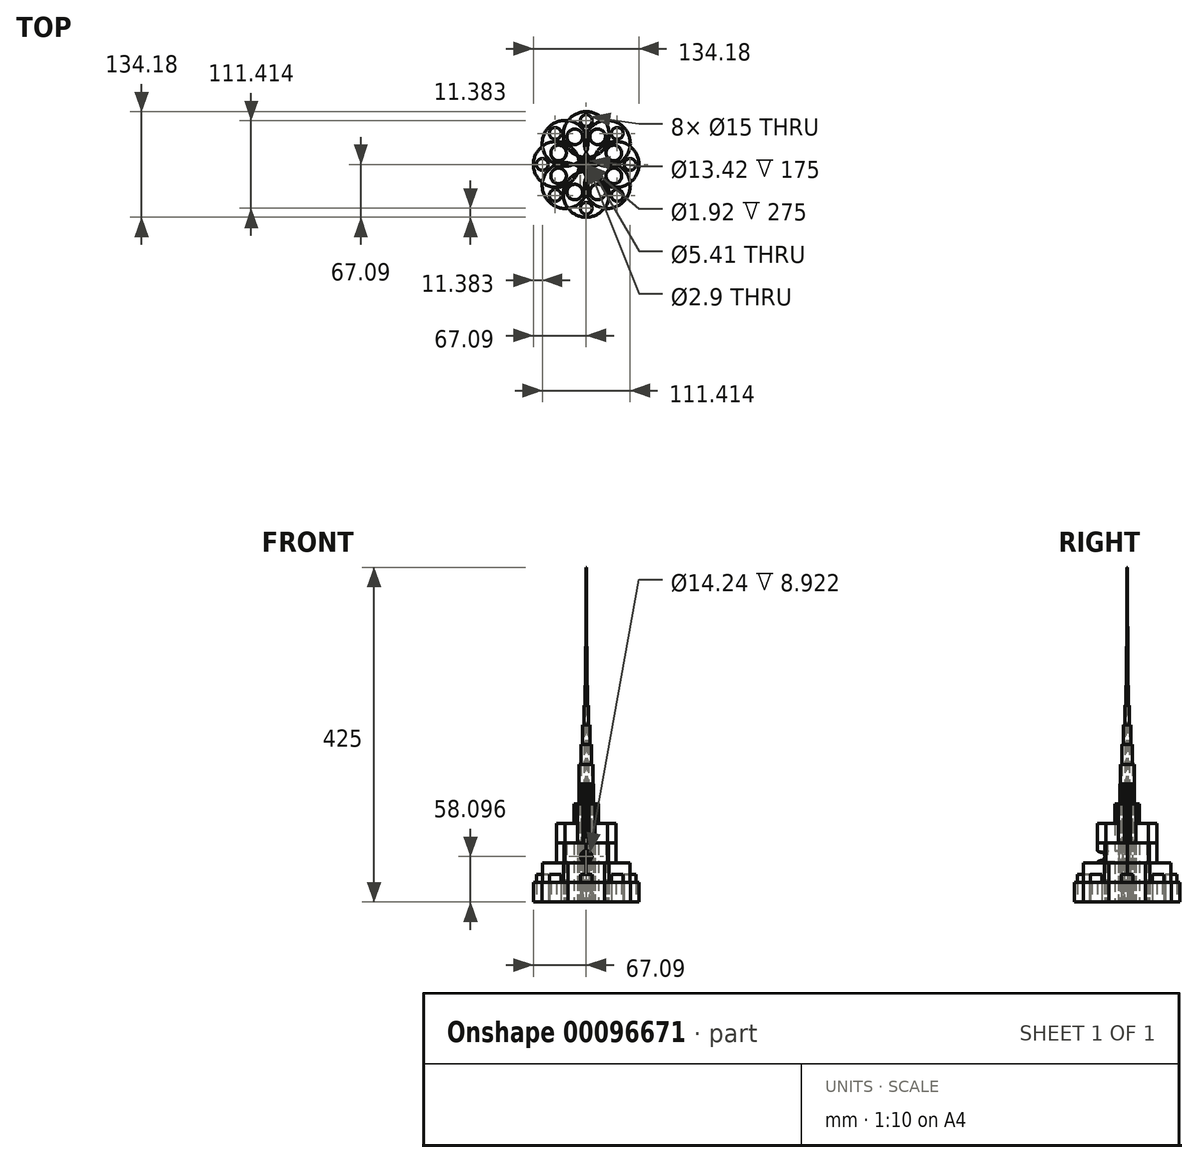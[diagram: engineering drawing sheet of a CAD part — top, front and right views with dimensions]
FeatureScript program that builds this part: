
annotation { "Feature Type Name" : "Feature", "Feature Type Description" : "" }
export const myFeature = defineFeature(function(context is Context, id is Id, definition is map)
    precondition{}
    {
        {
            var Q0;
            Q0=qCreatedBy(makeId("Top.planeOp"),FACE);
            var sketch = newSketch(context, id + "F0", { "sketchPlane" : qUnion([Q0])});
            skCircle(sketch, "E0", {"center": v(0, 0) * mm, "radius": 38 * mm});
            skPoint(sketch, "E1", {"position": v(-26.87, 26.87) * mm});
            skPoint(sketch, "E2", {"position": v(26.87, -26.87) * mm});
            skPoint(sketch, "E3", {"position": v(26.87, 26.87) * mm});
            skPoint(sketch, "E4", {"position": v(-26.87, -26.87) * mm});
            skPoint(sketch, "E5", {"position": v(0, 38) * mm});
            skPoint(sketch, "E6", {"position": v(0, -38) * mm});
            skPoint(sketch, "E7", {"position": v(38, 0) * mm});
            skPoint(sketch, "E8", {"position": v(-38, 0) * mm});
            skCircle(sketch, "E9", {"center": v(-26.87, 26.87) * mm, "radius": 29.08 * mm});
            skCircle(sketch, "E10", {"center": v(26.87, 26.87) * mm, "radius": 29.08 * mm});
            skCircle(sketch, "E11", {"center": v(38, 0) * mm, "radius": 29.08 * mm});
            skCircle(sketch, "E12", {"center": v(-26.87, -26.87) * mm, "radius": 29.08 * mm});
            skCircle(sketch, "E13", {"center": v(26.87, -26.87) * mm, "radius": 29.08 * mm});
            skCircle(sketch, "E14", {"center": v(0, -38) * mm, "radius": 29.08 * mm});
            skCircle(sketch, "E15", {"center": v(-38, 0) * mm, "radius": 29.08 * mm});
            skCircle(sketch, "E16", {"center": v(0, 38) * mm, "radius": 29.08 * mm});
            skCircle(sketch, "E17", {"center": v(0, 0) * mm, "radius": 8.92 * mm});
            skCircle(sketch, "E18", {"center": v(0, 0) * mm, "radius": 6.7 * mm});
            skCircle(sketch, "E19", {"center": v(0, 0) * mm, "radius": 4.58 * mm});
            skCircle(sketch, "E20", {"center": v(0, 0) * mm, "radius": 2.7 * mm});
            skCircle(sketch, "E21", {"center": v(0, 0) * mm, "radius": 1.45 * mm});
            skPoint(sketch, "E22", {"position": v(-23.07, 55.7) * mm});
            skPoint(sketch, "E23", {"position": v(23.07, 55.7) * mm});
            skPoint(sketch, "E24", {"position": v(55.7, 23.07) * mm});
            skPoint(sketch, "E25", {"position": v(55.7, -23.07) * mm});
            skPoint(sketch, "E26", {"position": v(23.07, -55.7) * mm});
            skPoint(sketch, "E27", {"position": v(-23.07, -55.7) * mm});
            skPoint(sketch, "E28", {"position": v(-55.7, -23.07) * mm});
            skPoint(sketch, "E29", {"position": v(-55.7, 23.07) * mm});
            skPoint(sketch, "E30", {"position": v(-14.54, 35.1) * mm});
            skPoint(sketch, "E31", {"position": v(14.54, 35.1) * mm});
            skPoint(sketch, "E32", {"position": v(35.1, 14.54) * mm});
            skPoint(sketch, "E33", {"position": v(35.1, -14.54) * mm});
            skPoint(sketch, "E34", {"position": v(14.54, -35.1) * mm});
            skPoint(sketch, "E35", {"position": v(-14.54, -35.1) * mm});
            skPoint(sketch, "E36", {"position": v(-35.1, -14.54) * mm});
            skPoint(sketch, "E37", {"position": v(-35.1, 14.54) * mm});
            skCircle(sketch, "E38", {"center": v(-35.1, 14.54) * mm, "radius": 9.89 * mm});
            skCircle(sketch, "E39", {"center": v(-14.54, 35.1) * mm, "radius": 9.89 * mm});
            skCircle(sketch, "E40", {"center": v(14.54, 35.1) * mm, "radius": 9.89 * mm});
            skCircle(sketch, "E41", {"center": v(35.1, 14.54) * mm, "radius": 9.89 * mm});
            skCircle(sketch, "E42", {"center": v(35.1, -14.54) * mm, "radius": 9.89 * mm});
            skCircle(sketch, "E43", {"center": v(14.54, -35.1) * mm, "radius": 9.89 * mm});
            skCircle(sketch, "E44", {"center": v(-14.54, -35.1) * mm, "radius": 9.89 * mm});
            skCircle(sketch, "E45", {"center": v(-35.1, -14.54) * mm, "radius": 9.89 * mm});
            skPoint(sketch, "E46", {"position": v(-39.4, 39.4) * mm});
            skPoint(sketch, "E47", {"position": v(0, 55.7) * mm});
            skPoint(sketch, "E48", {"position": v(39.4, 39.4) * mm});
            skPoint(sketch, "E49", {"position": v(55.7, 0) * mm});
            skPoint(sketch, "E50", {"position": v(39.4, -39.4) * mm});
            skPoint(sketch, "E51", {"position": v(0, -55.7) * mm});
            skPoint(sketch, "E52", {"position": v(-39.4, -39.4) * mm});
            skPoint(sketch, "E53", {"position": v(-55.7, 0) * mm});
            skCircle(sketch, "E54", {"center": v(-39.4, 39.4) * mm, "radius": 7.5 * mm});
            skCircle(sketch, "E55", {"center": v(0, 55.7) * mm, "radius": 7.5 * mm});
            skCircle(sketch, "E56", {"center": v(39.4, 39.4) * mm, "radius": 7.5 * mm});
            skCircle(sketch, "E57", {"center": v(55.7, 0) * mm, "radius": 7.5 * mm});
            skCircle(sketch, "E58", {"center": v(39.4, -39.4) * mm, "radius": 7.5 * mm});
            skCircle(sketch, "E59", {"center": v(0, -55.7) * mm, "radius": 7.5 * mm});
            skCircle(sketch, "E60", {"center": v(-39.4, -39.4) * mm, "radius": 7.5 * mm});
            skCircle(sketch, "E61", {"center": v(-55.7, 0) * mm, "radius": 7.5 * mm});
            skCircle(sketch, "E62", {"center": v(0, 0) * mm, "radius": 0.96 * mm});
            skCircle(sketch, "E63", {"center": v(0, 0) * mm, "radius": 0.76 * mm});
            skCircle(sketch, "E64", {"center": v(0, 0) * mm, "radius": 0.57 * mm});
            skCircle(sketch, "E65", {"center": v(0, -0.01) * mm, "radius": 0.41 * mm});
            skCircle(sketch, "E66", {"center": v(0, -0.01) * mm, "radius": 0.3 * mm});
            skCircle(sketch, "E67", {"center": v(0, -0.01) * mm, "radius": 0.19 * mm});
            skSolve(sketch);
        }
        {
            var Q0;
            {var subQ0=sQuery(id+"F0.wireOp",EDGE,"E16");var subQ1=sQuery(id+"F0.wireOp",EDGE,"E9");var subQ2=makeQuery(id+"F0.imprint","INTERSECT",VERTEX,{"disambiguationData":[OD(0.0)],"derivedFrom":[subQ1,subQ0]});Q0=makeQuery(id+"F0.imprint","IMPRINT",FACE,{"disambiguationData":[TD([[makeQuery(id+"F0.imprint","IMPRINT",EDGE,{"disambiguationData":[TD([[subQ2,-1.0]])],"derivedFrom":subQ1}),1.0]])]});}
            var Q1;
            {var subQ0=sQuery(id+"F0.wireOp",EDGE,"E16");var subQ1=sQuery(id+"F0.wireOp",EDGE,"E9");var subQ2=makeQuery(id+"F0.imprint","INTERSECT",VERTEX,{"disambiguationData":[OD(0.0)],"derivedFrom":[subQ1,subQ0]});Q1=makeQuery(id+"F0.imprint","IMPRINT",FACE,{"disambiguationData":[TD([[makeQuery(id+"F0.imprint","IMPRINT",EDGE,{"disambiguationData":[TD([[subQ2,1.0]])],"derivedFrom":subQ0}),1.0]])]});}
            var Q2;
            {var subQ0=sQuery(id+"F0.wireOp",EDGE,"E16");var subQ1=sQuery(id+"F0.wireOp",EDGE,"E10");var subQ2=makeQuery(id+"F0.imprint","INTERSECT",VERTEX,{"disambiguationData":[OD(0.0)],"derivedFrom":[subQ1,subQ0]});Q2=makeQuery(id+"F0.imprint","IMPRINT",FACE,{"disambiguationData":[TD([[makeQuery(id+"F0.imprint","IMPRINT",EDGE,{"disambiguationData":[TD([[subQ2,1.0]])],"derivedFrom":subQ1}),1.0]])]});}
            var Q3;
            {var subQ0=sQuery(id+"F0.wireOp",EDGE,"E11");var subQ1=sQuery(id+"F0.wireOp",EDGE,"E10");var subQ2=makeQuery(id+"F0.imprint","INTERSECT",VERTEX,{"disambiguationData":[OD(0.0)],"derivedFrom":[subQ1,subQ0]});Q3=makeQuery(id+"F0.imprint","IMPRINT",FACE,{"disambiguationData":[TD([[makeQuery(id+"F0.imprint","IMPRINT",EDGE,{"disambiguationData":[TD([[subQ2,1.0]])],"derivedFrom":subQ0}),1.0]])]});}
            var Q4;
            {var subQ0=sQuery(id+"F0.wireOp",EDGE,"E13");var subQ1=sQuery(id+"F0.wireOp",EDGE,"E11");var subQ2=makeQuery(id+"F0.imprint","INTERSECT",VERTEX,{"disambiguationData":[OD(0.0)],"derivedFrom":[subQ1,subQ0]});Q4=makeQuery(id+"F0.imprint","IMPRINT",FACE,{"disambiguationData":[TD([[makeQuery(id+"F0.imprint","IMPRINT",EDGE,{"disambiguationData":[TD([[subQ2,1.0]])],"derivedFrom":subQ0}),1.0]])]});}
            var Q5;
            {var subQ0=sQuery(id+"F0.wireOp",EDGE,"E14");var subQ1=sQuery(id+"F0.wireOp",EDGE,"E12");var subQ2=makeQuery(id+"F0.imprint","INTERSECT",VERTEX,{"disambiguationData":[OD(0.0)],"derivedFrom":[subQ1,subQ0]});Q5=makeQuery(id+"F0.imprint","IMPRINT",FACE,{"disambiguationData":[TD([[makeQuery(id+"F0.imprint","IMPRINT",EDGE,{"disambiguationData":[TD([[subQ2,-1.0]])],"derivedFrom":subQ0}),1.0]])]});}
            var Q6;
            {var subQ0=sQuery(id+"F0.wireOp",EDGE,"E15");var subQ1=sQuery(id+"F0.wireOp",EDGE,"E12");var subQ2=makeQuery(id+"F0.imprint","INTERSECT",VERTEX,{"disambiguationData":[OD(0.0)],"derivedFrom":[subQ1,subQ0]});Q6=makeQuery(id+"F0.imprint","IMPRINT",FACE,{"disambiguationData":[TD([[makeQuery(id+"F0.imprint","IMPRINT",EDGE,{"disambiguationData":[TD([[subQ2,-1.0]])],"derivedFrom":subQ1}),1.0]])]});}
            var Q7;
            {var subQ0=sQuery(id+"F0.wireOp",EDGE,"E15");var subQ1=sQuery(id+"F0.wireOp",EDGE,"E9");var subQ2=makeQuery(id+"F0.imprint","INTERSECT",VERTEX,{"disambiguationData":[OD(0.0)],"derivedFrom":[subQ1,subQ0]});Q7=makeQuery(id+"F0.imprint","IMPRINT",FACE,{"disambiguationData":[TD([[makeQuery(id+"F0.imprint","IMPRINT",EDGE,{"disambiguationData":[TD([[subQ2,-1.0]])],"derivedFrom":subQ0}),1.0]])]});}
            extrude(context, id + "F1", {"entities" : qUnion([Q0, Q1, Q2, Q3, Q4, Q5, Q6, Q7]), "depth" : 25 * mm});
        }
        {
            var Q0;
            {var subQ0=sQuery(id+"F0.wireOp",EDGE,"E9");var subQ3=sQuery(id+"F0.wireOp",EDGE,"E16");var subQ5=makeQuery(id+"F0.imprint","INTERSECT",VERTEX,{"disambiguationData":[OD(0.0)],"derivedFrom":[subQ0,subQ3]});Q0=makeQuery(id+"F0.imprint","IMPRINT",FACE,{"disambiguationData":[TD([[makeQuery(id+"F0.imprint","IMPRINT",EDGE,{"disambiguationData":[TD([[subQ5,1.0]])],"derivedFrom":subQ0}),1.0]])]});}
            var Q1;
            {var subQ0=sQuery(id+"F0.wireOp",EDGE,"E16");var subQ3=sQuery(id+"F0.wireOp",EDGE,"E10");var subQ5=makeQuery(id+"F0.imprint","INTERSECT",VERTEX,{"disambiguationData":[OD(0.0)],"derivedFrom":[subQ3,subQ0]});Q1=makeQuery(id+"F0.imprint","IMPRINT",FACE,{"disambiguationData":[TD([[makeQuery(id+"F0.imprint","IMPRINT",EDGE,{"disambiguationData":[TD([[subQ5,-1.0]])],"derivedFrom":subQ3}),1.0]])]});}
            var Q2;
            {var subQ0=sQuery(id+"F0.wireOp",EDGE,"E13");var subQ3=sQuery(id+"F0.wireOp",EDGE,"E11");var subQ5=makeQuery(id+"F0.imprint","INTERSECT",VERTEX,{"disambiguationData":[OD(0.0)],"derivedFrom":[subQ3,subQ0]});Q2=makeQuery(id+"F0.imprint","IMPRINT",FACE,{"disambiguationData":[TD([[makeQuery(id+"F0.imprint","IMPRINT",EDGE,{"disambiguationData":[TD([[subQ5,1.0]])],"derivedFrom":subQ3}),1.0]])]});}
            var Q3;
            {var subQ0=sQuery(id+"F0.wireOp",EDGE,"E11");var subQ3=sQuery(id+"F0.wireOp",EDGE,"E10");var subQ5=makeQuery(id+"F0.imprint","INTERSECT",VERTEX,{"disambiguationData":[OD(0.0)],"derivedFrom":[subQ3,subQ0]});Q3=makeQuery(id+"F0.imprint","IMPRINT",FACE,{"disambiguationData":[TD([[makeQuery(id+"F0.imprint","IMPRINT",EDGE,{"disambiguationData":[TD([[subQ5,1.0]])],"derivedFrom":subQ3}),1.0]])]});}
            var Q4;
            {var subQ0=sQuery(id+"F0.wireOp",EDGE,"E13");var subQ3=sQuery(id+"F0.wireOp",EDGE,"E14");var subQ5=makeQuery(id+"F0.imprint","INTERSECT",VERTEX,{"disambiguationData":[OD(0.0)],"derivedFrom":[subQ0,subQ3]});Q4=makeQuery(id+"F0.imprint","IMPRINT",FACE,{"disambiguationData":[TD([[makeQuery(id+"F0.imprint","IMPRINT",EDGE,{"disambiguationData":[TD([[subQ5,1.0]])],"derivedFrom":subQ0}),1.0]])]});}
            var Q5;
            {var subQ0=sQuery(id+"F0.wireOp",EDGE,"E14");var subQ3=sQuery(id+"F0.wireOp",EDGE,"E12");var subQ5=makeQuery(id+"F0.imprint","INTERSECT",VERTEX,{"disambiguationData":[OD(0.0)],"derivedFrom":[subQ3,subQ0]});Q5=makeQuery(id+"F0.imprint","IMPRINT",FACE,{"disambiguationData":[TD([[makeQuery(id+"F0.imprint","IMPRINT",EDGE,{"disambiguationData":[TD([[subQ5,-1.0]])],"derivedFrom":subQ3}),1.0]])]});}
            var Q6;
            {var subQ0=sQuery(id+"F0.wireOp",EDGE,"E12");var subQ3=sQuery(id+"F0.wireOp",EDGE,"E15");var subQ5=makeQuery(id+"F0.imprint","INTERSECT",VERTEX,{"disambiguationData":[OD(0.0)],"derivedFrom":[subQ0,subQ3]});Q6=makeQuery(id+"F0.imprint","IMPRINT",FACE,{"disambiguationData":[TD([[makeQuery(id+"F0.imprint","IMPRINT",EDGE,{"disambiguationData":[TD([[subQ5,1.0]])],"derivedFrom":subQ0}),1.0]])]});}
            var Q7;
            {var subQ0=sQuery(id+"F0.wireOp",EDGE,"E15");var subQ3=sQuery(id+"F0.wireOp",EDGE,"E9");var subQ5=makeQuery(id+"F0.imprint","INTERSECT",VERTEX,{"disambiguationData":[OD(0.0)],"derivedFrom":[subQ3,subQ0]});Q7=makeQuery(id+"F0.imprint","IMPRINT",FACE,{"disambiguationData":[TD([[makeQuery(id+"F0.imprint","IMPRINT",EDGE,{"disambiguationData":[TD([[subQ5,-1.0]])],"derivedFrom":subQ3}),1.0]])]});}
            extrude(context, id + "F2", {"entities" : qUnion([Q0, Q1, Q2, Q3, Q4, Q5, Q6, Q7]), "depth" : 50 * mm});
        }
        {
            var Q0;
            {var subQ0=sQuery(id+"F0.wireOp",EDGE,"E16");var subQ5=sQuery(id+"F0.wireOp",EDGE,"E9");var subQ6=makeQuery(id+"F0.imprint","INTERSECT",VERTEX,{"disambiguationData":[OD(1.0)],"derivedFrom":[subQ5,subQ0]});Q0=makeQuery(id+"F0.imprint","IMPRINT",FACE,{"disambiguationData":[TD([[makeQuery(id+"F0.imprint","IMPRINT",EDGE,{"disambiguationData":[TD([[subQ6,-1.0]])],"derivedFrom":subQ5}),1.0]])]});}
            var Q1;
            {var subQ1=sQuery(id+"F0.wireOp",EDGE,"E9");var subQ5=sQuery(id+"F0.wireOp",EDGE,"E12");var subQ6=makeQuery(id+"F0.imprint","INTERSECT",VERTEX,{"derivedFrom":[subQ1,subQ5]});Q1=makeQuery(id+"F0.imprint","IMPRINT",FACE,{"disambiguationData":[TD([[makeQuery(id+"F0.imprint","IMPRINT",EDGE,{"disambiguationData":[TD([[subQ6,-1.0]])],"derivedFrom":subQ1}),1.0]])]});}
            var Q2;
            {var subQ5=sQuery(id+"F0.wireOp",EDGE,"E12");var subQ6=sQuery(id+"F0.wireOp",EDGE,"E9");var subQ7=makeQuery(id+"F0.imprint","INTERSECT",VERTEX,{"derivedFrom":[subQ6,subQ5]});Q2=makeQuery(id+"F0.imprint","IMPRINT",FACE,{"disambiguationData":[TD([[makeQuery(id+"F0.imprint","IMPRINT",EDGE,{"disambiguationData":[TD([[subQ7,1.0]])],"derivedFrom":subQ5}),1.0]])]});}
            var Q3;
            {var subQ0=sQuery(id+"F0.wireOp",EDGE,"E14");var subQ1=sQuery(id+"F0.wireOp",EDGE,"E12");var subQ2=makeQuery(id+"F0.imprint","INTERSECT",VERTEX,{"disambiguationData":[OD(1.0)],"derivedFrom":[subQ1,subQ0]});Q3=makeQuery(id+"F0.imprint","IMPRINT",FACE,{"disambiguationData":[TD([[makeQuery(id+"F0.imprint","IMPRINT",EDGE,{"disambiguationData":[TD([[subQ2,1.0]])],"derivedFrom":subQ1}),1.0]])]});}
            var Q4;
            {var subQ0=sQuery(id+"F0.wireOp",EDGE,"E13");var subQ1=sQuery(id+"F0.wireOp",EDGE,"E12");var subQ2=makeQuery(id+"F0.imprint","INTERSECT",VERTEX,{"derivedFrom":[subQ1,subQ0]});Q4=makeQuery(id+"F0.imprint","IMPRINT",FACE,{"disambiguationData":[TD([[makeQuery(id+"F0.imprint","IMPRINT",EDGE,{"disambiguationData":[TD([[subQ2,1.0]])],"derivedFrom":subQ0}),1.0]])]});}
            var Q5;
            {var subQ0=sQuery(id+"F0.wireOp",EDGE,"E13");var subQ3=sQuery(id+"F0.wireOp",EDGE,"E11");var subQ4=makeQuery(id+"F0.imprint","INTERSECT",VERTEX,{"disambiguationData":[OD(1.0)],"derivedFrom":[subQ3,subQ0]});Q5=makeQuery(id+"F0.imprint","IMPRINT",FACE,{"disambiguationData":[TD([[makeQuery(id+"F0.imprint","IMPRINT",EDGE,{"disambiguationData":[TD([[subQ4,-1.0]])],"derivedFrom":subQ3}),1.0]])]});}
            var Q6;
            {var subQ1=sQuery(id+"F0.wireOp",EDGE,"E10");var subQ5=sQuery(id+"F0.wireOp",EDGE,"E11");var subQ6=makeQuery(id+"F0.imprint","INTERSECT",VERTEX,{"disambiguationData":[OD(1.0)],"derivedFrom":[subQ1,subQ5]});Q6=makeQuery(id+"F0.imprint","IMPRINT",FACE,{"disambiguationData":[TD([[makeQuery(id+"F0.imprint","IMPRINT",EDGE,{"disambiguationData":[TD([[subQ6,-1.0]])],"derivedFrom":subQ1}),1.0]])]});}
            var Q7;
            {var subQ5=sQuery(id+"F0.wireOp",EDGE,"E10");var subQ6=sQuery(id+"F0.wireOp",EDGE,"E9");var subQ7=makeQuery(id+"F0.imprint","INTERSECT",VERTEX,{"derivedFrom":[subQ6,subQ5]});Q7=makeQuery(id+"F0.imprint","IMPRINT",FACE,{"disambiguationData":[TD([[makeQuery(id+"F0.imprint","IMPRINT",EDGE,{"disambiguationData":[TD([[subQ7,-1.0]])],"derivedFrom":subQ5}),1.0]])]});}
            extrude(context, id + "F3", {"entities" : qUnion([Q0, Q1, Q2, Q3, Q4, Q5, Q6, Q7]), "depth" : 75 * mm});
        }
        {
            var Q0;
            {var subQ0=sQuery(id+"F0.wireOp",EDGE,"E10");var subQ1=sQuery(id+"F0.wireOp",EDGE,"E9");var subQ2=makeQuery(id+"F0.imprint","INTERSECT",VERTEX,{"derivedFrom":[subQ1,subQ0]});Q0=makeQuery(id+"F0.imprint","IMPRINT",FACE,{"disambiguationData":[TD([[makeQuery(id+"F0.imprint","IMPRINT",EDGE,{"disambiguationData":[TD([[subQ2,-1.0]])],"derivedFrom":subQ1}),1.0]])]});}
            var Q1;
            {var subQ0=sQuery(id+"F0.wireOp",EDGE,"E16");var subQ1=sQuery(id+"F0.wireOp",EDGE,"E15");var subQ2=makeQuery(id+"F0.imprint","INTERSECT",VERTEX,{"derivedFrom":[subQ1,subQ0]});Q1=makeQuery(id+"F0.imprint","IMPRINT",FACE,{"disambiguationData":[TD([[makeQuery(id+"F0.imprint","IMPRINT",EDGE,{"disambiguationData":[TD([[subQ2,-1.0]])],"derivedFrom":subQ1}),1.0]])]});}
            var Q2;
            {var subQ0=sQuery(id+"F0.wireOp",EDGE,"E12");var subQ1=sQuery(id+"F0.wireOp",EDGE,"E9");var subQ2=makeQuery(id+"F0.imprint","INTERSECT",VERTEX,{"derivedFrom":[subQ1,subQ0]});Q2=makeQuery(id+"F0.imprint","IMPRINT",FACE,{"disambiguationData":[TD([[makeQuery(id+"F0.imprint","IMPRINT",EDGE,{"disambiguationData":[TD([[subQ2,1.0]])],"derivedFrom":subQ1}),1.0]])]});}
            var Q3;
            {var subQ0=sQuery(id+"F0.wireOp",EDGE,"E15");var subQ1=sQuery(id+"F0.wireOp",EDGE,"E14");var subQ2=makeQuery(id+"F0.imprint","INTERSECT",VERTEX,{"derivedFrom":[subQ1,subQ0]});Q3=makeQuery(id+"F0.imprint","IMPRINT",FACE,{"disambiguationData":[TD([[makeQuery(id+"F0.imprint","IMPRINT",EDGE,{"disambiguationData":[TD([[subQ2,-1.0]])],"derivedFrom":subQ1}),1.0]])]});}
            var Q4;
            {var subQ0=sQuery(id+"F0.wireOp",EDGE,"E13");var subQ1=sQuery(id+"F0.wireOp",EDGE,"E12");var subQ2=makeQuery(id+"F0.imprint","INTERSECT",VERTEX,{"derivedFrom":[subQ1,subQ0]});Q4=makeQuery(id+"F0.imprint","IMPRINT",FACE,{"disambiguationData":[TD([[makeQuery(id+"F0.imprint","IMPRINT",EDGE,{"disambiguationData":[TD([[subQ2,1.0]])],"derivedFrom":subQ1}),1.0]])]});}
            var Q5;
            {var subQ0=sQuery(id+"F0.wireOp",EDGE,"E14");var subQ1=sQuery(id+"F0.wireOp",EDGE,"E11");var subQ2=makeQuery(id+"F0.imprint","INTERSECT",VERTEX,{"derivedFrom":[subQ1,subQ0]});Q5=makeQuery(id+"F0.imprint","IMPRINT",FACE,{"disambiguationData":[TD([[makeQuery(id+"F0.imprint","IMPRINT",EDGE,{"disambiguationData":[TD([[subQ2,-1.0]])],"derivedFrom":subQ1}),1.0]])]});}
            var Q6;
            {var subQ0=sQuery(id+"F0.wireOp",EDGE,"E13");var subQ1=sQuery(id+"F0.wireOp",EDGE,"E10");var subQ2=makeQuery(id+"F0.imprint","INTERSECT",VERTEX,{"derivedFrom":[subQ1,subQ0]});Q6=makeQuery(id+"F0.imprint","IMPRINT",FACE,{"disambiguationData":[TD([[makeQuery(id+"F0.imprint","IMPRINT",EDGE,{"disambiguationData":[TD([[subQ2,-1.0]])],"derivedFrom":subQ1}),1.0]])]});}
            var Q7;
            {var subQ0=sQuery(id+"F0.wireOp",EDGE,"E16");var subQ1=sQuery(id+"F0.wireOp",EDGE,"E11");var subQ2=makeQuery(id+"F0.imprint","INTERSECT",VERTEX,{"derivedFrom":[subQ1,subQ0]});Q7=makeQuery(id+"F0.imprint","IMPRINT",FACE,{"disambiguationData":[TD([[makeQuery(id+"F0.imprint","IMPRINT",EDGE,{"disambiguationData":[TD([[subQ2,1.0]])],"derivedFrom":subQ1}),1.0]])]});}
            extrude(context, id + "F4", {"entities" : qUnion([Q0, Q1, Q2, Q3, Q4, Q5, Q6, Q7]), "depth" : 100 * mm});
        }
        {
            var Q0;
            {var subQ0=sQuery(id+"F0.wireOp",EDGE,"E15");var subQ1=sQuery(id+"F0.wireOp",EDGE,"E9");var subQ2=makeQuery(id+"F0.imprint","INTERSECT",VERTEX,{"disambiguationData":[OD(1.0)],"derivedFrom":[subQ1,subQ0]});Q0=makeQuery(id+"F0.imprint","IMPRINT",FACE,{"disambiguationData":[TD([[makeQuery(id+"F0.imprint","IMPRINT",EDGE,{"disambiguationData":[TD([[subQ2,-1.0]])],"derivedFrom":subQ1}),1.0]])]});}
            var Q1;
            {var subQ0=sQuery(id+"F0.wireOp",EDGE,"E16");var subQ1=sQuery(id+"F0.wireOp",EDGE,"E9");var subQ2=makeQuery(id+"F0.imprint","INTERSECT",VERTEX,{"disambiguationData":[OD(1.0)],"derivedFrom":[subQ1,subQ0]});Q1=makeQuery(id+"F0.imprint","IMPRINT",FACE,{"disambiguationData":[TD([[makeQuery(id+"F0.imprint","IMPRINT",EDGE,{"disambiguationData":[TD([[subQ2,-1.0]])],"derivedFrom":subQ1}),-1.0]])]});}
            var Q2;
            {var subQ0=sQuery(id+"F0.wireOp",EDGE,"E16");var subQ1=sQuery(id+"F0.wireOp",EDGE,"E10");var subQ2=makeQuery(id+"F0.imprint","INTERSECT",VERTEX,{"disambiguationData":[OD(1.0)],"derivedFrom":[subQ1,subQ0]});Q2=makeQuery(id+"F0.imprint","IMPRINT",FACE,{"disambiguationData":[TD([[makeQuery(id+"F0.imprint","IMPRINT",EDGE,{"disambiguationData":[TD([[subQ2,-1.0]])],"derivedFrom":subQ1}),1.0]])]});}
            var Q3;
            {var subQ0=sQuery(id+"F0.wireOp",EDGE,"E11");var subQ1=sQuery(id+"F0.wireOp",EDGE,"E10");var subQ2=makeQuery(id+"F0.imprint","INTERSECT",VERTEX,{"disambiguationData":[OD(1.0)],"derivedFrom":[subQ1,subQ0]});Q3=makeQuery(id+"F0.imprint","IMPRINT",FACE,{"disambiguationData":[TD([[makeQuery(id+"F0.imprint","IMPRINT",EDGE,{"disambiguationData":[TD([[subQ2,-1.0]])],"derivedFrom":subQ1}),-1.0]])]});}
            var Q4;
            {var subQ0=sQuery(id+"F0.wireOp",EDGE,"E13");var subQ1=sQuery(id+"F0.wireOp",EDGE,"E11");var subQ2=makeQuery(id+"F0.imprint","INTERSECT",VERTEX,{"disambiguationData":[OD(1.0)],"derivedFrom":[subQ1,subQ0]});Q4=makeQuery(id+"F0.imprint","IMPRINT",FACE,{"disambiguationData":[TD([[makeQuery(id+"F0.imprint","IMPRINT",EDGE,{"disambiguationData":[TD([[subQ2,-1.0]])],"derivedFrom":subQ1}),-1.0]])]});}
            var Q5;
            {var subQ0=sQuery(id+"F0.wireOp",EDGE,"E14");var subQ1=sQuery(id+"F0.wireOp",EDGE,"E12");var subQ2=makeQuery(id+"F0.imprint","INTERSECT",VERTEX,{"disambiguationData":[OD(1.0)],"derivedFrom":[subQ1,subQ0]});Q5=makeQuery(id+"F0.imprint","IMPRINT",FACE,{"disambiguationData":[TD([[makeQuery(id+"F0.imprint","IMPRINT",EDGE,{"disambiguationData":[TD([[subQ2,1.0]])],"derivedFrom":subQ1}),-1.0]])]});}
            var Q6;
            {var subQ0=sQuery(id+"F0.wireOp",EDGE,"E14");var subQ1=sQuery(id+"F0.wireOp",EDGE,"E12");var subQ2=makeQuery(id+"F0.imprint","INTERSECT",VERTEX,{"disambiguationData":[OD(1.0)],"derivedFrom":[subQ1,subQ0]});Q6=makeQuery(id+"F0.imprint","IMPRINT",FACE,{"disambiguationData":[TD([[makeQuery(id+"F0.imprint","IMPRINT",EDGE,{"disambiguationData":[TD([[subQ2,-1.0]])],"derivedFrom":subQ1}),1.0]])]});}
            var Q7;
            {var subQ0=sQuery(id+"F0.wireOp",EDGE,"E12");var subQ1=sQuery(id+"F0.wireOp",EDGE,"E9");var subQ2=makeQuery(id+"F0.imprint","INTERSECT",VERTEX,{"derivedFrom":[subQ1,subQ0]});Q7=makeQuery(id+"F0.imprint","IMPRINT",FACE,{"disambiguationData":[TD([[makeQuery(id+"F0.imprint","IMPRINT",EDGE,{"disambiguationData":[TD([[subQ2,-1.0]])],"derivedFrom":subQ1}),-1.0]])]});}
            extrude(context, id + "F5", {"entities" : qUnion([Q0, Q1, Q2, Q3, Q4, Q5, Q6, Q7]), "depth" : 125 * mm});
        }
        {
            var Q0;
            {var subQ0=sQuery(id+"F0.wireOp",EDGE,"E17");var subQ1=sQuery(id+"F0.wireOp",EDGE,"E9");var subQ2=makeQuery(id+"F0.imprint","INTERSECT",VERTEX,{"derivedFrom":[subQ1,subQ0]});Q0=makeQuery(id+"F0.imprint","IMPRINT",FACE,{"disambiguationData":[TD([[makeQuery(id+"F0.imprint","IMPRINT",EDGE,{"disambiguationData":[TD([[subQ2,-1.0]])],"derivedFrom":subQ1}),-1.0]])]});}
            var Q1;
            {var subQ0=sQuery(id+"F0.wireOp",EDGE,"E16");var subQ1=sQuery(id+"F0.wireOp",EDGE,"E10");var subQ2=makeQuery(id+"F0.imprint","INTERSECT",VERTEX,{"disambiguationData":[OD(1.0)],"derivedFrom":[subQ1,subQ0]});Q1=makeQuery(id+"F0.imprint","IMPRINT",FACE,{"disambiguationData":[TD([[makeQuery(id+"F0.imprint","IMPRINT",EDGE,{"disambiguationData":[TD([[subQ2,-1.0]])],"derivedFrom":subQ1}),-1.0]])]});}
            var Q2;
            {var subQ0=sQuery(id+"F0.wireOp",EDGE,"E15");var subQ1=sQuery(id+"F0.wireOp",EDGE,"E9");var subQ2=makeQuery(id+"F0.imprint","INTERSECT",VERTEX,{"disambiguationData":[OD(1.0)],"derivedFrom":[subQ1,subQ0]});Q2=makeQuery(id+"F0.imprint","IMPRINT",FACE,{"disambiguationData":[TD([[makeQuery(id+"F0.imprint","IMPRINT",EDGE,{"disambiguationData":[TD([[subQ2,-1.0]])],"derivedFrom":subQ1}),-1.0]])]});}
            var Q3;
            {var subQ0=sQuery(id+"F0.wireOp",EDGE,"E17");var subQ1=sQuery(id+"F0.wireOp",EDGE,"E12");var subQ2=makeQuery(id+"F0.imprint","INTERSECT",VERTEX,{"derivedFrom":[subQ1,subQ0]});Q3=makeQuery(id+"F0.imprint","IMPRINT",FACE,{"disambiguationData":[TD([[makeQuery(id+"F0.imprint","IMPRINT",EDGE,{"disambiguationData":[TD([[subQ2,-1.0]])],"derivedFrom":subQ1}),-1.0]])]});}
            var Q4;
            {var subQ0=sQuery(id+"F0.wireOp",EDGE,"E14");var subQ1=sQuery(id+"F0.wireOp",EDGE,"E12");var subQ2=makeQuery(id+"F0.imprint","INTERSECT",VERTEX,{"disambiguationData":[OD(1.0)],"derivedFrom":[subQ1,subQ0]});Q4=makeQuery(id+"F0.imprint","IMPRINT",FACE,{"disambiguationData":[TD([[makeQuery(id+"F0.imprint","IMPRINT",EDGE,{"disambiguationData":[TD([[subQ2,-1.0]])],"derivedFrom":subQ1}),-1.0]])]});}
            var Q5;
            {var subQ0=sQuery(id+"F0.wireOp",EDGE,"E17");var subQ1=sQuery(id+"F0.wireOp",EDGE,"E13");var subQ2=makeQuery(id+"F0.imprint","INTERSECT",VERTEX,{"derivedFrom":[subQ1,subQ0]});Q5=makeQuery(id+"F0.imprint","IMPRINT",FACE,{"disambiguationData":[TD([[makeQuery(id+"F0.imprint","IMPRINT",EDGE,{"disambiguationData":[TD([[subQ2,-1.0]])],"derivedFrom":subQ1}),-1.0]])]});}
            var Q6;
            {var subQ0=sQuery(id+"F0.wireOp",EDGE,"E17");var subQ1=sQuery(id+"F0.wireOp",EDGE,"E11");var subQ2=makeQuery(id+"F0.imprint","INTERSECT",VERTEX,{"derivedFrom":[subQ1,subQ0]});Q6=makeQuery(id+"F0.imprint","IMPRINT",FACE,{"disambiguationData":[TD([[makeQuery(id+"F0.imprint","IMPRINT",EDGE,{"disambiguationData":[TD([[subQ2,-1.0]])],"derivedFrom":subQ1}),-1.0]])]});}
            var Q7;
            {var subQ0=sQuery(id+"F0.wireOp",EDGE,"E17");var subQ1=sQuery(id+"F0.wireOp",EDGE,"E10");var subQ2=makeQuery(id+"F0.imprint","INTERSECT",VERTEX,{"derivedFrom":[subQ1,subQ0]});Q7=makeQuery(id+"F0.imprint","IMPRINT",FACE,{"disambiguationData":[TD([[makeQuery(id+"F0.imprint","IMPRINT",EDGE,{"disambiguationData":[TD([[subQ2,-1.0]])],"derivedFrom":subQ1}),-1.0]])]});}
            extrude(context, id + "F6", {"entities" : qUnion([Q0, Q1, Q2, Q3, Q4, Q5, Q6, Q7]), "depth" : 150 * mm});
        }
        {
            var Q0;
            {var subQ0=sQuery(id+"F0.wireOp",EDGE,"E17");var subQ4=makeQuery(id+"F0.imprint","INTERSECT",VERTEX,{"derivedFrom":[sQuery(id+"F0.wireOp",EDGE,"E10"),subQ0]});Q0=makeQuery(id+"F0.imprint","IMPRINT",FACE,{"disambiguationData":[TD([[makeQuery(id+"F0.imprint","IMPRINT",EDGE,{"disambiguationData":[TD([[subQ4,1.0]])],"derivedFrom":subQ0}),1.0]])]});}
            extrude(context, id + "F7", {"entities" : qUnion([Q0]), "depth" : 175 * mm});
        }
        {
            var Q0;
            Q0=makeQuery(id+"F0.imprint","IMPRINT",FACE,{"disambiguationData":[TD([[makeQuery(id+"F0.imprint","IMPRINT",EDGE,{"derivedFrom":sQuery(id+"F0.wireOp",EDGE,"E18")}),1.0]])]});
            extrude(context, id + "F8", {"entities" : qUnion([Q0]), "depth" : 200 * mm});
        }
        {
            var Q0;
            Q0=makeQuery(id+"F0.imprint","IMPRINT",FACE,{"disambiguationData":[TD([[makeQuery(id+"F0.imprint","IMPRINT",EDGE,{"derivedFrom":sQuery(id+"F0.wireOp",EDGE,"E19")}),1.0]])]});
            extrude(context, id + "F9", {"entities" : qUnion([Q0]), "operationType" : NewBodyOperationType.ADD, "depth" : 225 * mm});
        }
        {
            var Q0;
            Q0=makeQuery(id+"F0.imprint","IMPRINT",FACE,{"disambiguationData":[TD([[makeQuery(id+"F0.imprint","IMPRINT",EDGE,{"derivedFrom":sQuery(id+"F0.wireOp",EDGE,"E20")}),1.0]])]});
            extrude(context, id + "F10", {"entities" : qUnion([Q0]), "depth" : 250 * mm});
        }
        {
            var Q0;
            Q0=makeQuery(id+"F0.imprint","IMPRINT",FACE,{"disambiguationData":[TD([[makeQuery(id+"F0.imprint","IMPRINT",EDGE,{"derivedFrom":sQuery(id+"F0.wireOp",EDGE,"E21")}),1.0]])]});
            extrude(context, id + "F11", {"entities" : qUnion([Q0]), "depth" : 275 * mm});
        }
        {
            var Q0;
            Q0=makeQuery(id+"F0.imprint","IMPRINT",FACE,{"disambiguationData":[TD([[makeQuery(id+"F0.imprint","IMPRINT",EDGE,{"derivedFrom":sQuery(id+"F0.wireOp",EDGE,"E54")}),1.0]])]});
            var Q1;
            Q1=makeQuery(id+"F0.imprint","IMPRINT",FACE,{"disambiguationData":[TD([[makeQuery(id+"F0.imprint","IMPRINT",EDGE,{"derivedFrom":sQuery(id+"F0.wireOp",EDGE,"E55")}),1.0]])]});
            var Q2;
            Q2=makeQuery(id+"F0.imprint","IMPRINT",FACE,{"disambiguationData":[TD([[makeQuery(id+"F0.imprint","IMPRINT",EDGE,{"derivedFrom":sQuery(id+"F0.wireOp",EDGE,"E56")}),1.0]])]});
            var Q3;
            Q3=makeQuery(id+"F0.imprint","IMPRINT",FACE,{"disambiguationData":[TD([[makeQuery(id+"F0.imprint","IMPRINT",EDGE,{"derivedFrom":sQuery(id+"F0.wireOp",EDGE,"E57")}),1.0]])]});
            var Q4;
            Q4=makeQuery(id+"F0.imprint","IMPRINT",FACE,{"disambiguationData":[TD([[makeQuery(id+"F0.imprint","IMPRINT",EDGE,{"derivedFrom":sQuery(id+"F0.wireOp",EDGE,"E58")}),1.0]])]});
            var Q5;
            Q5=makeQuery(id+"F0.imprint","IMPRINT",FACE,{"disambiguationData":[TD([[makeQuery(id+"F0.imprint","IMPRINT",EDGE,{"derivedFrom":sQuery(id+"F0.wireOp",EDGE,"E59")}),1.0]])]});
            var Q6;
            Q6=makeQuery(id+"F0.imprint","IMPRINT",FACE,{"disambiguationData":[TD([[makeQuery(id+"F0.imprint","IMPRINT",EDGE,{"derivedFrom":sQuery(id+"F0.wireOp",EDGE,"E60")}),1.0]])]});
            var Q7;
            Q7=makeQuery(id+"F0.imprint","IMPRINT",FACE,{"disambiguationData":[TD([[makeQuery(id+"F0.imprint","IMPRINT",EDGE,{"derivedFrom":sQuery(id+"F0.wireOp",EDGE,"E61")}),1.0]])]});
            extrude(context, id + "F12", {"entities" : qUnion([Q0, Q1, Q2, Q3, Q4, Q5, Q6, Q7]), "depth" : 35 * mm});
        }
        {
            var Q0;
            {var subQ0=sQuery(id+"F0.wireOp",EDGE,"E38");var subQ1=sQuery(id+"F0.wireOp",EDGE,"E0");var subQ2=makeQuery(id+"F0.imprint","INTERSECT",VERTEX,{"disambiguationData":[OD(0.0)],"derivedFrom":[subQ1,subQ0]});Q0=makeQuery(id+"F0.imprint","IMPRINT",FACE,{"disambiguationData":[TD([[makeQuery(id+"F0.imprint","IMPRINT",EDGE,{"disambiguationData":[TD([[subQ2,-1.0]])],"derivedFrom":subQ1}),-1.0]])]});}
            var Q1;
            {var subQ0=sQuery(id+"F0.wireOp",EDGE,"E38");var subQ1=sQuery(id+"F0.wireOp",EDGE,"E0");var subQ2=makeQuery(id+"F0.imprint","INTERSECT",VERTEX,{"disambiguationData":[OD(0.0)],"derivedFrom":[subQ1,subQ0]});Q1=makeQuery(id+"F0.imprint","IMPRINT",FACE,{"disambiguationData":[TD([[makeQuery(id+"F0.imprint","IMPRINT",EDGE,{"disambiguationData":[TD([[subQ2,-1.0]])],"derivedFrom":subQ1}),1.0]])]});}
            var Q2;
            {var subQ0=sQuery(id+"F0.wireOp",EDGE,"E39");var subQ1=sQuery(id+"F0.wireOp",EDGE,"E0");var subQ2=makeQuery(id+"F0.imprint","INTERSECT",VERTEX,{"disambiguationData":[OD(0.0)],"derivedFrom":[subQ1,subQ0]});Q2=makeQuery(id+"F0.imprint","IMPRINT",FACE,{"disambiguationData":[TD([[makeQuery(id+"F0.imprint","IMPRINT",EDGE,{"disambiguationData":[TD([[subQ2,-1.0]])],"derivedFrom":subQ1}),-1.0]])]});}
            var Q3;
            {var subQ0=sQuery(id+"F0.wireOp",EDGE,"E39");var subQ1=sQuery(id+"F0.wireOp",EDGE,"E0");var subQ2=makeQuery(id+"F0.imprint","INTERSECT",VERTEX,{"disambiguationData":[OD(0.0)],"derivedFrom":[subQ1,subQ0]});Q3=makeQuery(id+"F0.imprint","IMPRINT",FACE,{"disambiguationData":[TD([[makeQuery(id+"F0.imprint","IMPRINT",EDGE,{"disambiguationData":[TD([[subQ2,-1.0]])],"derivedFrom":subQ1}),1.0]])]});}
            var Q4;
            {var subQ0=sQuery(id+"F0.wireOp",EDGE,"E40");var subQ1=sQuery(id+"F0.wireOp",EDGE,"E0");var subQ2=makeQuery(id+"F0.imprint","INTERSECT",VERTEX,{"disambiguationData":[OD(0.0)],"derivedFrom":[subQ1,subQ0]});Q4=makeQuery(id+"F0.imprint","IMPRINT",FACE,{"disambiguationData":[TD([[makeQuery(id+"F0.imprint","IMPRINT",EDGE,{"disambiguationData":[TD([[subQ2,-1.0]])],"derivedFrom":subQ1}),-1.0]])]});}
            var Q5;
            {var subQ0=sQuery(id+"F0.wireOp",EDGE,"E40");var subQ1=sQuery(id+"F0.wireOp",EDGE,"E0");var subQ2=makeQuery(id+"F0.imprint","INTERSECT",VERTEX,{"disambiguationData":[OD(0.0)],"derivedFrom":[subQ1,subQ0]});Q5=makeQuery(id+"F0.imprint","IMPRINT",FACE,{"disambiguationData":[TD([[makeQuery(id+"F0.imprint","IMPRINT",EDGE,{"disambiguationData":[TD([[subQ2,-1.0]])],"derivedFrom":subQ1}),1.0]])]});}
            var Q6;
            {var subQ0=sQuery(id+"F0.wireOp",EDGE,"E41");var subQ1=sQuery(id+"F0.wireOp",EDGE,"E0");var subQ2=makeQuery(id+"F0.imprint","INTERSECT",VERTEX,{"disambiguationData":[OD(0.0)],"derivedFrom":[subQ1,subQ0]});Q6=makeQuery(id+"F0.imprint","IMPRINT",FACE,{"disambiguationData":[TD([[makeQuery(id+"F0.imprint","IMPRINT",EDGE,{"disambiguationData":[TD([[subQ2,-1.0]])],"derivedFrom":subQ1}),-1.0]])]});}
            var Q7;
            {var subQ0=sQuery(id+"F0.wireOp",EDGE,"E41");var subQ1=sQuery(id+"F0.wireOp",EDGE,"E0");var subQ2=makeQuery(id+"F0.imprint","INTERSECT",VERTEX,{"disambiguationData":[OD(0.0)],"derivedFrom":[subQ1,subQ0]});Q7=makeQuery(id+"F0.imprint","IMPRINT",FACE,{"disambiguationData":[TD([[makeQuery(id+"F0.imprint","IMPRINT",EDGE,{"disambiguationData":[TD([[subQ2,-1.0]])],"derivedFrom":subQ1}),1.0]])]});}
            var Q8;
            {var subQ0=sQuery(id+"F0.wireOp",EDGE,"E42");var subQ1=sQuery(id+"F0.wireOp",EDGE,"E0");var subQ2=makeQuery(id+"F0.imprint","INTERSECT",VERTEX,{"disambiguationData":[OD(0.0)],"derivedFrom":[subQ1,subQ0]});Q8=makeQuery(id+"F0.imprint","IMPRINT",FACE,{"disambiguationData":[TD([[makeQuery(id+"F0.imprint","IMPRINT",EDGE,{"disambiguationData":[TD([[subQ2,-1.0]])],"derivedFrom":subQ1}),-1.0]])]});}
            var Q9;
            {var subQ0=sQuery(id+"F0.wireOp",EDGE,"E43");var subQ1=sQuery(id+"F0.wireOp",EDGE,"E0");var subQ2=makeQuery(id+"F0.imprint","INTERSECT",VERTEX,{"disambiguationData":[OD(0.0)],"derivedFrom":[subQ1,subQ0]});Q9=makeQuery(id+"F0.imprint","IMPRINT",FACE,{"disambiguationData":[TD([[makeQuery(id+"F0.imprint","IMPRINT",EDGE,{"disambiguationData":[TD([[subQ2,-1.0]])],"derivedFrom":subQ1}),-1.0]])]});}
            var Q10;
            {var subQ0=sQuery(id+"F0.wireOp",EDGE,"E43");var subQ1=sQuery(id+"F0.wireOp",EDGE,"E0");var subQ2=makeQuery(id+"F0.imprint","INTERSECT",VERTEX,{"disambiguationData":[OD(0.0)],"derivedFrom":[subQ1,subQ0]});Q10=makeQuery(id+"F0.imprint","IMPRINT",FACE,{"disambiguationData":[TD([[makeQuery(id+"F0.imprint","IMPRINT",EDGE,{"disambiguationData":[TD([[subQ2,-1.0]])],"derivedFrom":subQ1}),1.0]])]});}
            var Q11;
            {var subQ0=sQuery(id+"F0.wireOp",EDGE,"E42");var subQ1=sQuery(id+"F0.wireOp",EDGE,"E0");var subQ2=makeQuery(id+"F0.imprint","INTERSECT",VERTEX,{"disambiguationData":[OD(0.0)],"derivedFrom":[subQ1,subQ0]});Q11=makeQuery(id+"F0.imprint","IMPRINT",FACE,{"disambiguationData":[TD([[makeQuery(id+"F0.imprint","IMPRINT",EDGE,{"disambiguationData":[TD([[subQ2,-1.0]])],"derivedFrom":subQ1}),1.0]])]});}
            var Q12;
            {var subQ0=sQuery(id+"F0.wireOp",EDGE,"E44");var subQ1=sQuery(id+"F0.wireOp",EDGE,"E0");var subQ2=makeQuery(id+"F0.imprint","INTERSECT",VERTEX,{"disambiguationData":[OD(0.0)],"derivedFrom":[subQ1,subQ0]});Q12=makeQuery(id+"F0.imprint","IMPRINT",FACE,{"disambiguationData":[TD([[makeQuery(id+"F0.imprint","IMPRINT",EDGE,{"disambiguationData":[TD([[subQ2,-1.0]])],"derivedFrom":subQ1}),1.0]])]});}
            var Q13;
            {var subQ0=sQuery(id+"F0.wireOp",EDGE,"E44");var subQ1=sQuery(id+"F0.wireOp",EDGE,"E0");var subQ2=makeQuery(id+"F0.imprint","INTERSECT",VERTEX,{"disambiguationData":[OD(0.0)],"derivedFrom":[subQ1,subQ0]});Q13=makeQuery(id+"F0.imprint","IMPRINT",FACE,{"disambiguationData":[TD([[makeQuery(id+"F0.imprint","IMPRINT",EDGE,{"disambiguationData":[TD([[subQ2,-1.0]])],"derivedFrom":subQ1}),-1.0]])]});}
            var Q14;
            {var subQ0=sQuery(id+"F0.wireOp",EDGE,"E45");var subQ1=sQuery(id+"F0.wireOp",EDGE,"E0");var subQ2=makeQuery(id+"F0.imprint","INTERSECT",VERTEX,{"disambiguationData":[OD(0.0)],"derivedFrom":[subQ1,subQ0]});Q14=makeQuery(id+"F0.imprint","IMPRINT",FACE,{"disambiguationData":[TD([[makeQuery(id+"F0.imprint","IMPRINT",EDGE,{"disambiguationData":[TD([[subQ2,-1.0]])],"derivedFrom":subQ1}),-1.0]])]});}
            var Q15;
            {var subQ0=sQuery(id+"F0.wireOp",EDGE,"E45");var subQ1=sQuery(id+"F0.wireOp",EDGE,"E0");var subQ2=makeQuery(id+"F0.imprint","INTERSECT",VERTEX,{"disambiguationData":[OD(0.0)],"derivedFrom":[subQ1,subQ0]});Q15=makeQuery(id+"F0.imprint","IMPRINT",FACE,{"disambiguationData":[TD([[makeQuery(id+"F0.imprint","IMPRINT",EDGE,{"disambiguationData":[TD([[subQ2,-1.0]])],"derivedFrom":subQ1}),1.0]])]});}
            extrude(context, id + "F13", {"entities" : qUnion([Q0, Q1, Q2, Q3, Q4, Q5, Q6, Q7, Q8, Q9, Q10, Q11, Q12, Q13, Q14, Q15]), "depth" : 25 * mm});
        }
        {
            var Q0;
            {var subQ0=sQuery(id+"F0.wireOp",EDGE,"E43");var subQ1=sQuery(id+"F0.wireOp",EDGE,"E0");Q0=makeQuery(id+"F3.opExtrude","SWEPT_EDGE",EDGE,{"disambiguationData":[OSD([subQ1,subQ0]),TDD([makeQuery(id+"F0.imprint","INTERSECT",VERTEX,{"disambiguationData":[OD(0.0)],"derivedFrom":[subQ1,subQ0]})])]});}
            var Q1;
            {var subQ0=sQuery(id+"F0.wireOp",EDGE,"E43");var subQ1=sQuery(id+"F0.wireOp",EDGE,"E0");Q1=makeQuery(id+"F3.opExtrude","SWEPT_EDGE",EDGE,{"disambiguationData":[OSD([subQ1,subQ0]),TDD([makeQuery(id+"F0.imprint","INTERSECT",VERTEX,{"disambiguationData":[OD(1.0)],"derivedFrom":[subQ1,subQ0]})])]});}
            fillet(context, id + "F14", {"entities" : qUnion([Q0, Q1]), "radius" : 5 * mm, "tangentPropagation" : true, "allowEdgeOverflow" : false});
        }
        {
            var Q0;
            {var subQ0=sQuery(id+"F0.wireOp",EDGE,"E42");var subQ1=sQuery(id+"F0.wireOp",EDGE,"E0");Q0=makeQuery(id+"F3.opExtrude","SWEPT_EDGE",EDGE,{"disambiguationData":[OSD([subQ1,subQ0]),TDD([makeQuery(id+"F0.imprint","INTERSECT",VERTEX,{"disambiguationData":[OD(0.0)],"derivedFrom":[subQ1,subQ0]})])]});}
            var Q1;
            {var subQ0=sQuery(id+"F0.wireOp",EDGE,"E42");var subQ1=sQuery(id+"F0.wireOp",EDGE,"E0");Q1=makeQuery(id+"F3.opExtrude","SWEPT_EDGE",EDGE,{"disambiguationData":[OSD([subQ1,subQ0]),TDD([makeQuery(id+"F0.imprint","INTERSECT",VERTEX,{"disambiguationData":[OD(1.0)],"derivedFrom":[subQ1,subQ0]})])]});}
            fillet(context, id + "F15", {"entities" : qUnion([Q0, Q1]), "radius" : 5 * mm, "tangentPropagation" : true, "allowEdgeOverflow" : false});
        }
        {
            var Q0;
            {var subQ0=sQuery(id+"F0.wireOp",EDGE,"E41");var subQ1=sQuery(id+"F0.wireOp",EDGE,"E0");Q0=makeQuery(id+"F3.opExtrude","SWEPT_EDGE",EDGE,{"disambiguationData":[OSD([subQ1,subQ0]),TDD([makeQuery(id+"F0.imprint","INTERSECT",VERTEX,{"disambiguationData":[OD(0.0)],"derivedFrom":[subQ1,subQ0]})])]});}
            var Q1;
            {var subQ0=sQuery(id+"F0.wireOp",EDGE,"E41");var subQ1=sQuery(id+"F0.wireOp",EDGE,"E0");Q1=makeQuery(id+"F3.opExtrude","SWEPT_EDGE",EDGE,{"disambiguationData":[OSD([subQ1,subQ0]),TDD([makeQuery(id+"F0.imprint","INTERSECT",VERTEX,{"disambiguationData":[OD(1.0)],"derivedFrom":[subQ1,subQ0]})])]});}
            var Q2;
            {var subQ0=sQuery(id+"F0.wireOp",EDGE,"E40");var subQ1=sQuery(id+"F0.wireOp",EDGE,"E0");Q2=makeQuery(id+"F3.opExtrude","SWEPT_EDGE",EDGE,{"disambiguationData":[OSD([subQ1,subQ0]),TDD([makeQuery(id+"F0.imprint","INTERSECT",VERTEX,{"disambiguationData":[OD(0.0)],"derivedFrom":[subQ1,subQ0]})])]});}
            var Q3;
            {var subQ0=sQuery(id+"F0.wireOp",EDGE,"E40");var subQ1=sQuery(id+"F0.wireOp",EDGE,"E0");Q3=makeQuery(id+"F3.opExtrude","SWEPT_EDGE",EDGE,{"disambiguationData":[OSD([subQ1,subQ0]),TDD([makeQuery(id+"F0.imprint","INTERSECT",VERTEX,{"disambiguationData":[OD(1.0)],"derivedFrom":[subQ1,subQ0]})])]});}
            fillet(context, id + "F16", {"entities" : qUnion([Q0, Q1, Q2, Q3]), "radius" : 5 * mm, "tangentPropagation" : true, "allowEdgeOverflow" : false});
        }
        {
            var Q0;
            {var subQ0=sQuery(id+"F0.wireOp",EDGE,"E39");var subQ1=sQuery(id+"F0.wireOp",EDGE,"E0");Q0=makeQuery(id+"F3.opExtrude","SWEPT_EDGE",EDGE,{"disambiguationData":[OSD([subQ1,subQ0]),TDD([makeQuery(id+"F0.imprint","INTERSECT",VERTEX,{"disambiguationData":[OD(1.0)],"derivedFrom":[subQ1,subQ0]})])]});}
            var Q1;
            {var subQ0=sQuery(id+"F0.wireOp",EDGE,"E39");var subQ1=sQuery(id+"F0.wireOp",EDGE,"E0");Q1=makeQuery(id+"F3.opExtrude","SWEPT_EDGE",EDGE,{"disambiguationData":[OSD([subQ1,subQ0]),TDD([makeQuery(id+"F0.imprint","INTERSECT",VERTEX,{"disambiguationData":[OD(0.0)],"derivedFrom":[subQ1,subQ0]})])]});}
            var Q2;
            {var subQ0=sQuery(id+"F0.wireOp",EDGE,"E38");var subQ1=sQuery(id+"F0.wireOp",EDGE,"E0");Q2=makeQuery(id+"F3.opExtrude","SWEPT_EDGE",EDGE,{"disambiguationData":[OSD([subQ1,subQ0]),TDD([makeQuery(id+"F0.imprint","INTERSECT",VERTEX,{"disambiguationData":[OD(0.0)],"derivedFrom":[subQ1,subQ0]})])]});}
            var Q3;
            {var subQ0=sQuery(id+"F0.wireOp",EDGE,"E38");var subQ1=sQuery(id+"F0.wireOp",EDGE,"E0");Q3=makeQuery(id+"F3.opExtrude","SWEPT_EDGE",EDGE,{"disambiguationData":[OSD([subQ1,subQ0]),TDD([makeQuery(id+"F0.imprint","INTERSECT",VERTEX,{"disambiguationData":[OD(1.0)],"derivedFrom":[subQ1,subQ0]})])]});}
            fillet(context, id + "F17", {"entities" : qUnion([Q0, Q1, Q2, Q3]), "radius" : 5 * mm, "tangentPropagation" : true, "allowEdgeOverflow" : false});
        }
        {
            var Q0;
            {var subQ0=sQuery(id+"F0.wireOp",EDGE,"E45");var subQ1=sQuery(id+"F0.wireOp",EDGE,"E0");Q0=makeQuery(id+"F3.opExtrude","SWEPT_EDGE",EDGE,{"disambiguationData":[OSD([subQ1,subQ0]),TDD([makeQuery(id+"F0.imprint","INTERSECT",VERTEX,{"disambiguationData":[OD(0.0)],"derivedFrom":[subQ1,subQ0]})])]});}
            var Q1;
            {var subQ0=sQuery(id+"F0.wireOp",EDGE,"E45");var subQ1=sQuery(id+"F0.wireOp",EDGE,"E0");Q1=makeQuery(id+"F3.opExtrude","SWEPT_EDGE",EDGE,{"disambiguationData":[OSD([subQ1,subQ0]),TDD([makeQuery(id+"F0.imprint","INTERSECT",VERTEX,{"disambiguationData":[OD(1.0)],"derivedFrom":[subQ1,subQ0]})])]});}
            var Q2;
            {var subQ0=sQuery(id+"F0.wireOp",EDGE,"E44");var subQ1=sQuery(id+"F0.wireOp",EDGE,"E0");Q2=makeQuery(id+"F3.opExtrude","SWEPT_EDGE",EDGE,{"disambiguationData":[OSD([subQ1,subQ0]),TDD([makeQuery(id+"F0.imprint","INTERSECT",VERTEX,{"disambiguationData":[OD(0.0)],"derivedFrom":[subQ1,subQ0]})])]});}
            var Q3;
            {var subQ0=sQuery(id+"F0.wireOp",EDGE,"E44");var subQ1=sQuery(id+"F0.wireOp",EDGE,"E0");Q3=makeQuery(id+"F3.opExtrude","SWEPT_EDGE",EDGE,{"disambiguationData":[OSD([subQ1,subQ0]),TDD([makeQuery(id+"F0.imprint","INTERSECT",VERTEX,{"disambiguationData":[OD(1.0)],"derivedFrom":[subQ1,subQ0]})])]});}
            fillet(context, id + "F18", {"entities" : qUnion([Q0, Q1, Q2, Q3]), "radius" : 5 * mm, "tangentPropagation" : true, "allowEdgeOverflow" : false});
        }
        {
            var Q0;
            {var subQ0=sQuery(id+"F0.wireOp",EDGE,"E45");var subQ1=sQuery(id+"F0.wireOp",EDGE,"E0");Q0=makeQuery(id+"F2.opExtrude","SWEPT_EDGE",EDGE,{"disambiguationData":[OSD([subQ1,subQ0]),TDD([makeQuery(id+"F0.imprint","INTERSECT",VERTEX,{"disambiguationData":[OD(0.0)],"derivedFrom":[subQ1,subQ0]})])]});}
            var Q1;
            {var subQ0=sQuery(id+"F0.wireOp",EDGE,"E45");var subQ1=sQuery(id+"F0.wireOp",EDGE,"E0");Q1=makeQuery(id+"F2.opExtrude","SWEPT_EDGE",EDGE,{"disambiguationData":[OSD([subQ1,subQ0]),TDD([makeQuery(id+"F0.imprint","INTERSECT",VERTEX,{"disambiguationData":[OD(1.0)],"derivedFrom":[subQ1,subQ0]})])]});}
            fillet(context, id + "F19", {"entities" : qUnion([Q0, Q1]), "radius" : 5 * mm, "tangentPropagation" : true, "allowEdgeOverflow" : false});
        }
        {
            var Q0;
            {var subQ0=sQuery(id+"F0.wireOp",EDGE,"E38");var subQ1=sQuery(id+"F0.wireOp",EDGE,"E0");Q0=makeQuery(id+"F2.opExtrude","SWEPT_EDGE",EDGE,{"disambiguationData":[OSD([subQ1,subQ0]),TDD([makeQuery(id+"F0.imprint","INTERSECT",VERTEX,{"disambiguationData":[OD(0.0)],"derivedFrom":[subQ1,subQ0]})])]});}
            var Q1;
            {var subQ0=sQuery(id+"F0.wireOp",EDGE,"E38");var subQ1=sQuery(id+"F0.wireOp",EDGE,"E0");Q1=makeQuery(id+"F2.opExtrude","SWEPT_EDGE",EDGE,{"disambiguationData":[OSD([subQ1,subQ0]),TDD([makeQuery(id+"F0.imprint","INTERSECT",VERTEX,{"disambiguationData":[OD(1.0)],"derivedFrom":[subQ1,subQ0]})])]});}
            fillet(context, id + "F20", {"entities" : qUnion([Q0, Q1]), "radius" : 5 * mm, "tangentPropagation" : true, "allowEdgeOverflow" : false});
        }
        {
            var Q0;
            {var subQ0=sQuery(id+"F0.wireOp",EDGE,"E39");var subQ1=sQuery(id+"F0.wireOp",EDGE,"E0");Q0=makeQuery(id+"F2.opExtrude","SWEPT_EDGE",EDGE,{"disambiguationData":[OSD([subQ1,subQ0]),TDD([makeQuery(id+"F0.imprint","INTERSECT",VERTEX,{"disambiguationData":[OD(0.0)],"derivedFrom":[subQ1,subQ0]})])]});}
            var Q1;
            {var subQ0=sQuery(id+"F0.wireOp",EDGE,"E39");var subQ1=sQuery(id+"F0.wireOp",EDGE,"E0");Q1=makeQuery(id+"F2.opExtrude","SWEPT_EDGE",EDGE,{"disambiguationData":[OSD([subQ1,subQ0]),TDD([makeQuery(id+"F0.imprint","INTERSECT",VERTEX,{"disambiguationData":[OD(1.0)],"derivedFrom":[subQ1,subQ0]})])]});}
            fillet(context, id + "F21", {"entities" : qUnion([Q0, Q1]), "radius" : 5 * mm, "tangentPropagation" : true, "allowEdgeOverflow" : false});
        }
        {
            var Q0;
            {var subQ0=sQuery(id+"F0.wireOp",EDGE,"E40");var subQ1=sQuery(id+"F0.wireOp",EDGE,"E0");Q0=makeQuery(id+"F2.opExtrude","SWEPT_EDGE",EDGE,{"disambiguationData":[OSD([subQ1,subQ0]),TDD([makeQuery(id+"F0.imprint","INTERSECT",VERTEX,{"disambiguationData":[OD(1.0)],"derivedFrom":[subQ1,subQ0]})])]});}
            var Q1;
            {var subQ0=sQuery(id+"F0.wireOp",EDGE,"E40");var subQ1=sQuery(id+"F0.wireOp",EDGE,"E0");Q1=makeQuery(id+"F2.opExtrude","SWEPT_EDGE",EDGE,{"disambiguationData":[OSD([subQ1,subQ0]),TDD([makeQuery(id+"F0.imprint","INTERSECT",VERTEX,{"disambiguationData":[OD(0.0)],"derivedFrom":[subQ1,subQ0]})])]});}
            var Q2;
            {var subQ0=sQuery(id+"F0.wireOp",EDGE,"E41");var subQ1=sQuery(id+"F0.wireOp",EDGE,"E0");Q2=makeQuery(id+"F2.opExtrude","SWEPT_EDGE",EDGE,{"disambiguationData":[OSD([subQ1,subQ0]),TDD([makeQuery(id+"F0.imprint","INTERSECT",VERTEX,{"disambiguationData":[OD(1.0)],"derivedFrom":[subQ1,subQ0]})])]});}
            var Q3;
            {var subQ0=sQuery(id+"F0.wireOp",EDGE,"E41");var subQ1=sQuery(id+"F0.wireOp",EDGE,"E0");Q3=makeQuery(id+"F2.opExtrude","SWEPT_EDGE",EDGE,{"disambiguationData":[OSD([subQ1,subQ0]),TDD([makeQuery(id+"F0.imprint","INTERSECT",VERTEX,{"disambiguationData":[OD(0.0)],"derivedFrom":[subQ1,subQ0]})])]});}
            fillet(context, id + "F22", {"entities" : qUnion([Q0, Q1, Q2, Q3]), "radius" : 5 * mm, "tangentPropagation" : true, "allowEdgeOverflow" : false});
        }
        {
            var Q0;
            {var subQ0=sQuery(id+"F0.wireOp",EDGE,"E42");var subQ1=sQuery(id+"F0.wireOp",EDGE,"E0");Q0=makeQuery(id+"F2.opExtrude","SWEPT_EDGE",EDGE,{"disambiguationData":[OSD([subQ1,subQ0]),TDD([makeQuery(id+"F0.imprint","INTERSECT",VERTEX,{"disambiguationData":[OD(1.0)],"derivedFrom":[subQ1,subQ0]})])]});}
            var Q1;
            {var subQ0=sQuery(id+"F0.wireOp",EDGE,"E42");var subQ1=sQuery(id+"F0.wireOp",EDGE,"E0");Q1=makeQuery(id+"F2.opExtrude","SWEPT_EDGE",EDGE,{"disambiguationData":[OSD([subQ1,subQ0]),TDD([makeQuery(id+"F0.imprint","INTERSECT",VERTEX,{"disambiguationData":[OD(0.0)],"derivedFrom":[subQ1,subQ0]})])]});}
            var Q2;
            {var subQ0=sQuery(id+"F0.wireOp",EDGE,"E43");var subQ1=sQuery(id+"F0.wireOp",EDGE,"E0");Q2=makeQuery(id+"F2.opExtrude","SWEPT_EDGE",EDGE,{"disambiguationData":[OSD([subQ1,subQ0]),TDD([makeQuery(id+"F0.imprint","INTERSECT",VERTEX,{"disambiguationData":[OD(0.0)],"derivedFrom":[subQ1,subQ0]})])]});}
            var Q3;
            {var subQ0=sQuery(id+"F0.wireOp",EDGE,"E43");var subQ1=sQuery(id+"F0.wireOp",EDGE,"E0");Q3=makeQuery(id+"F2.opExtrude","SWEPT_EDGE",EDGE,{"disambiguationData":[OSD([subQ1,subQ0]),TDD([makeQuery(id+"F0.imprint","INTERSECT",VERTEX,{"disambiguationData":[OD(1.0)],"derivedFrom":[subQ1,subQ0]})])]});}
            var Q4;
            {var subQ0=sQuery(id+"F0.wireOp",EDGE,"E44");var subQ1=sQuery(id+"F0.wireOp",EDGE,"E0");Q4=makeQuery(id+"F2.opExtrude","SWEPT_EDGE",EDGE,{"disambiguationData":[OSD([subQ1,subQ0]),TDD([makeQuery(id+"F0.imprint","INTERSECT",VERTEX,{"disambiguationData":[OD(0.0)],"derivedFrom":[subQ1,subQ0]})])]});}
            var Q5;
            {var subQ0=sQuery(id+"F0.wireOp",EDGE,"E44");var subQ1=sQuery(id+"F0.wireOp",EDGE,"E0");Q5=makeQuery(id+"F2.opExtrude","SWEPT_EDGE",EDGE,{"disambiguationData":[OSD([subQ1,subQ0]),TDD([makeQuery(id+"F0.imprint","INTERSECT",VERTEX,{"disambiguationData":[OD(1.0)],"derivedFrom":[subQ1,subQ0]})])]});}
            fillet(context, id + "F23", {"entities" : qUnion([Q0, Q1, Q2, Q3, Q4, Q5]), "radius" : 5 * mm, "tangentPropagation" : true, "allowEdgeOverflow" : false});
        }
        {
            var Q0;
            Q0=makeQuery(id+"F0.imprint","IMPRINT",FACE,{"disambiguationData":[TD([[makeQuery(id+"F0.imprint","IMPRINT",EDGE,{"derivedFrom":sQuery(id+"F0.wireOp",EDGE,"E62")}),1.0]])]});
            extrude(context, id + "F24", {"entities" : qUnion([Q0]), "depth" : 300 * mm});
        }
        {
            var Q0;
            Q0=makeQuery(id+"F0.imprint","IMPRINT",FACE,{"disambiguationData":[TD([[makeQuery(id+"F0.imprint","IMPRINT",EDGE,{"derivedFrom":sQuery(id+"F0.wireOp",EDGE,"E63")}),1.0]])]});
            extrude(context, id + "F25", {"entities" : qUnion([Q0]), "operationType" : NewBodyOperationType.ADD, "depth" : 325 * mm});
        }
        {
            var Q0;
            Q0=makeQuery(id+"F0.imprint","IMPRINT",FACE,{"disambiguationData":[TD([[makeQuery(id+"F0.imprint","IMPRINT",EDGE,{"derivedFrom":sQuery(id+"F0.wireOp",EDGE,"E64")}),1.0]])]});
            extrude(context, id + "F26", {"entities" : qUnion([Q0]), "operationType" : NewBodyOperationType.ADD, "depth" : 350 * mm});
        }
        {
            var Q0;
            Q0=makeQuery(id+"F0.imprint","IMPRINT",FACE,{"disambiguationData":[TD([[makeQuery(id+"F0.imprint","IMPRINT",EDGE,{"derivedFrom":sQuery(id+"F0.wireOp",EDGE,"E65")}),1.0]])]});
            extrude(context, id + "F27", {"entities" : qUnion([Q0]), "operationType" : NewBodyOperationType.ADD, "depth" : 375 * mm});
        }
        {
            var Q0;
            Q0=makeQuery(id+"F0.imprint","IMPRINT",FACE,{"disambiguationData":[TD([[makeQuery(id+"F0.imprint","IMPRINT",EDGE,{"derivedFrom":sQuery(id+"F0.wireOp",EDGE,"E66")}),1.0]])]});
            extrude(context, id + "F28", {"entities" : qUnion([Q0]), "operationType" : NewBodyOperationType.ADD, "depth" : 400 * mm});
        }
        {
            var Q0;
            Q0=makeQuery(id+"F0.imprint","IMPRINT",FACE,{"disambiguationData":[TD([[makeQuery(id+"F0.imprint","IMPRINT",EDGE,{"derivedFrom":sQuery(id+"F0.wireOp",EDGE,"E67")}),1.0]])]});
            extrude(context, id + "F29", {"entities" : qUnion([Q0]), "operationType" : NewBodyOperationType.ADD, "depth" : 425 * mm});
        }
        {
            var Q0;
            Q0=qCreatedBy(makeId("Front.planeOp"),FACE);
            var sketch = newSketch(context, id + "F30", { "sketchPlane" : qUnion([Q0])});
            skCircle(sketch, "E68", {"center": v(0, 58.1) * mm, "radius": 7.12 * mm});
            skSolve(sketch);
        }
        {
            var Q0;
            Q0 = qSketchRegion(id + "F30", true);
            extrude(context, id + "F31", {"entities" : qUnion([Q0]), "operationType" : NewBodyOperationType.REMOVE, "endBound" : BoundingType.THROUGH_ALL, "depth" : 25 * mm});
        }
    });
